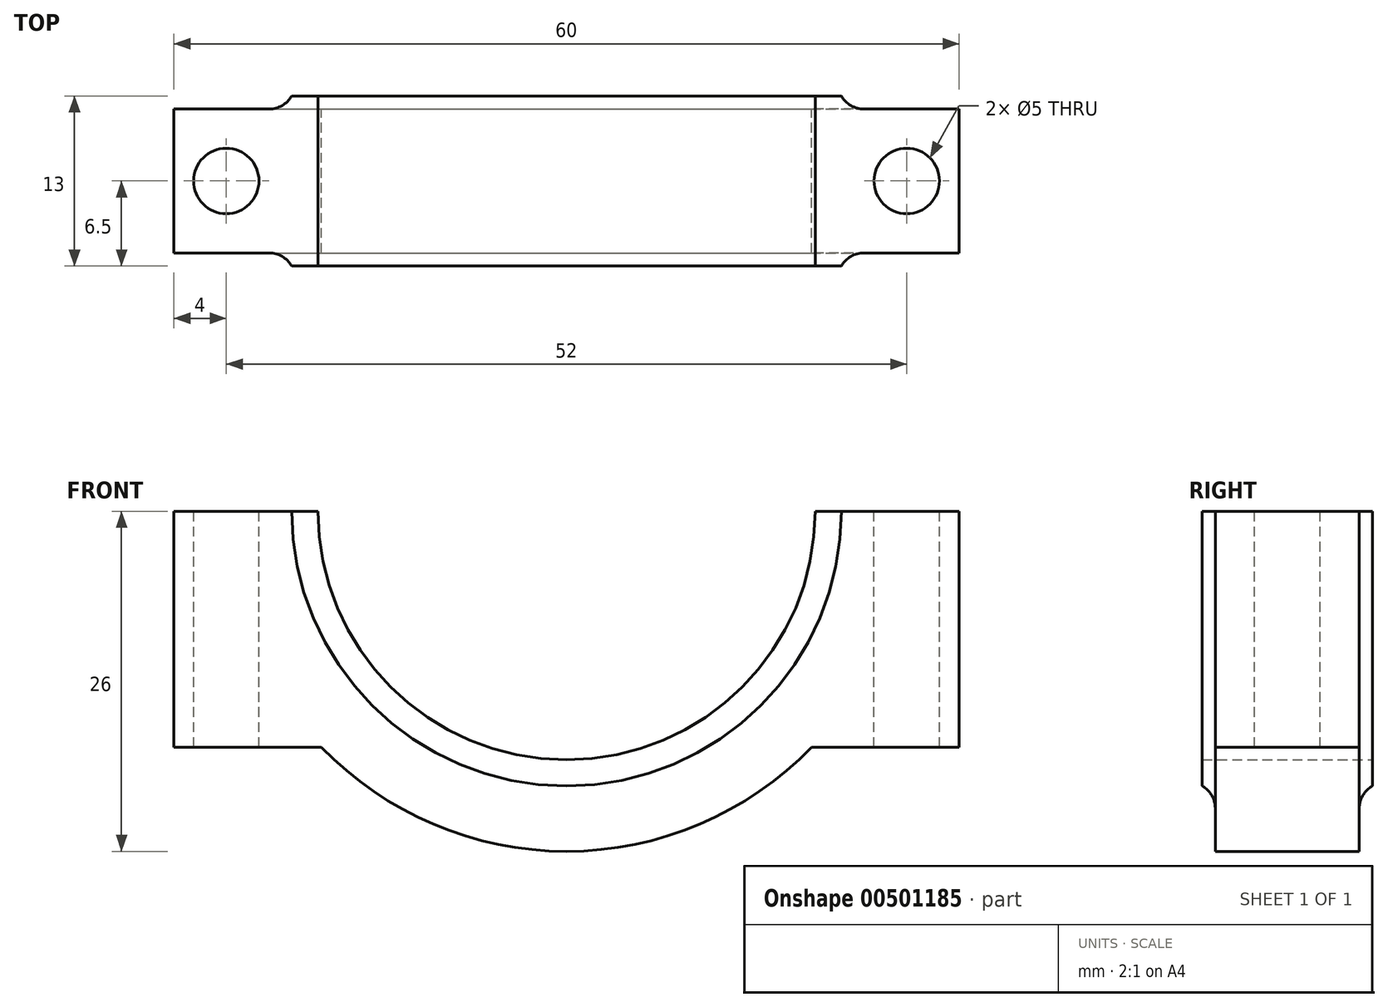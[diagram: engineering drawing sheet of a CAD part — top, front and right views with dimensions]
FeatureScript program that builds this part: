
annotation { "Feature Type Name" : "Feature", "Feature Type Description" : "" }
export const myFeature = defineFeature(function(context is Context, id is Id, definition is map)
    precondition{}
    {
        {
            var Q0;
            Q0=qCreatedBy(makeId("Front.planeOp"),FACE);
            var sketch = newSketch(context, id + "F0", { "sketchPlane" : qUnion([Q0])});
            skArc(sketch, "E0", {"start": v(-19, 0) * mm, "mid": v(0, -19) * mm, "end": v(19, 0) * mm});
            skLineSegment(sketch, "E1", {"start": v(-30, 0) * mm, "end": v(-19, 0) * mm});
            skLineSegment(sketch, "E2", {"start": v(30, 0) * mm, "end": v(30, -18.03) * mm});
            skLineSegment(sketch, "E3", {"start": v(-30, -18.03) * mm, "end": v(-30, 0) * mm});
            skLineSegment(sketch, "E4.trimOffspring", {"start": v(19, 0) * mm, "end": v(30, 0) * mm});
            skArc(sketch, "E5", {"start": v(-18.73, -18.03) * mm, "mid": v(0, -26) * mm, "end": v(18.73, -18.03) * mm});
            skLineSegment(sketch, "E6", {"start": v(-30, -18.03) * mm, "end": v(-18.73, -18.03) * mm});
            skLineSegment(sketch, "E7", {"start": v(30, -18.03) * mm, "end": v(18.73, -18.03) * mm});
            skArc(sketch, "E8", {"start": v(-21, 0) * mm, "mid": v(0, -21) * mm, "end": v(21, 0) * mm});
            skSolve(sketch);
        }
        {
            var Q0;
            Q0 = qSketchRegion(id + "F0", true);
            extrude(context, id + "F1", {"entities" : qUnion([Q0]), "endBound" : BoundingType.SYMMETRIC, "depth" : 11 * mm});
        }
        {
            var Q0;
            {var subQ0=sQuery(id+"F0.wireOp",EDGE,"E0");Q0=makeQuery(id+"F0.imprint","IMPRINT",FACE,{"disambiguationData":[TD([[makeQuery(id+"F0.imprint","IMPRINT",EDGE,{"derivedFrom":subQ0}),-1.0]])]});}
            extrude(context, id + "F2", {"entities" : qUnion([Q0]), "operationType" : NewBodyOperationType.ADD, "endBound" : BoundingType.SYMMETRIC, "depth" : 13 * mm});
        }
        {
            var Q0;
            Q0=makeQuery(id+"F2.boolean.opBoolean","INTERSECT",EDGE,{"derivedFrom":[makeQuery(id+"F1.opExtrude","CAP_FACE",FACE,{"disambiguationData":[OSD([sQuery(id+"F0.wireOp",EDGE,"E0"),sQuery(id+"F0.wireOp",EDGE,"E1"),sQuery(id+"F0.wireOp",EDGE,"E2"),sQuery(id+"F0.wireOp",EDGE,"E3"),sQuery(id+"F0.wireOp",EDGE,"E4.trimOffspring"),sQuery(id+"F0.wireOp",EDGE,"E5"),sQuery(id+"F0.wireOp",EDGE,"E6"),sQuery(id+"F0.wireOp",EDGE,"E7")])],"isStart":true}),makeQuery(id+"F2.opExtrude","SWEPT_FACE",FACE,{"disambiguationData":[OSD([sQuery(id+"F0.wireOp",EDGE,"E8")])]})]});
            var Q1;
            Q1=makeQuery(id+"F2.boolean.opBoolean","INTERSECT",EDGE,{"derivedFrom":[makeQuery(id+"F1.opExtrude","CAP_FACE",FACE,{"disambiguationData":[OSD([sQuery(id+"F0.wireOp",EDGE,"E0"),sQuery(id+"F0.wireOp",EDGE,"E1"),sQuery(id+"F0.wireOp",EDGE,"E2"),sQuery(id+"F0.wireOp",EDGE,"E3"),sQuery(id+"F0.wireOp",EDGE,"E4.trimOffspring"),sQuery(id+"F0.wireOp",EDGE,"E5"),sQuery(id+"F0.wireOp",EDGE,"E6"),sQuery(id+"F0.wireOp",EDGE,"E7")])],"isStart":false}),makeQuery(id+"F2.opExtrude","SWEPT_FACE",FACE,{"disambiguationData":[OSD([sQuery(id+"F0.wireOp",EDGE,"E8")])]})]});
            fillet(context, id + "F3", {"entities" : qUnion([Q0, Q1]), "radius" : 2 * mm, "tangentPropagation" : true, "allowEdgeOverflow" : false});
        }
        {
            var Q0;
            Q0=qCreatedBy(makeId("Top.planeOp"),FACE);
            var sketch = newSketch(context, id + "F4", { "sketchPlane" : qUnion([Q0])});
            skCircle(sketch, "E9", {"center": v(-26, 0) * mm, "radius": 2.5 * mm});
            skCircle(sketch, "E10", {"center": v(26, 0) * mm, "radius": 2.5 * mm});
            skSolve(sketch);
        }
        {
            var Q0;
            Q0=makeQuery(id+"F4.imprint","IMPRINT",FACE,{"disambiguationData":[TD([[makeQuery(id+"F4.imprint","IMPRINT",EDGE,{"derivedFrom":sQuery(id+"F4.wireOp",EDGE,"E9")}),1.0]])]});
            var Q1;
            Q1=makeQuery(id+"F4.imprint","IMPRINT",FACE,{"disambiguationData":[TD([[makeQuery(id+"F4.imprint","IMPRINT",EDGE,{"derivedFrom":sQuery(id+"F4.wireOp",EDGE,"E10")}),1.0]])]});
            extrude(context, id + "F5", {"entities" : qUnion([Q0, Q1]), "operationType" : NewBodyOperationType.REMOVE, "oppositeDirection" : true, "depth" : 25.4 * mm});
        }
    });
